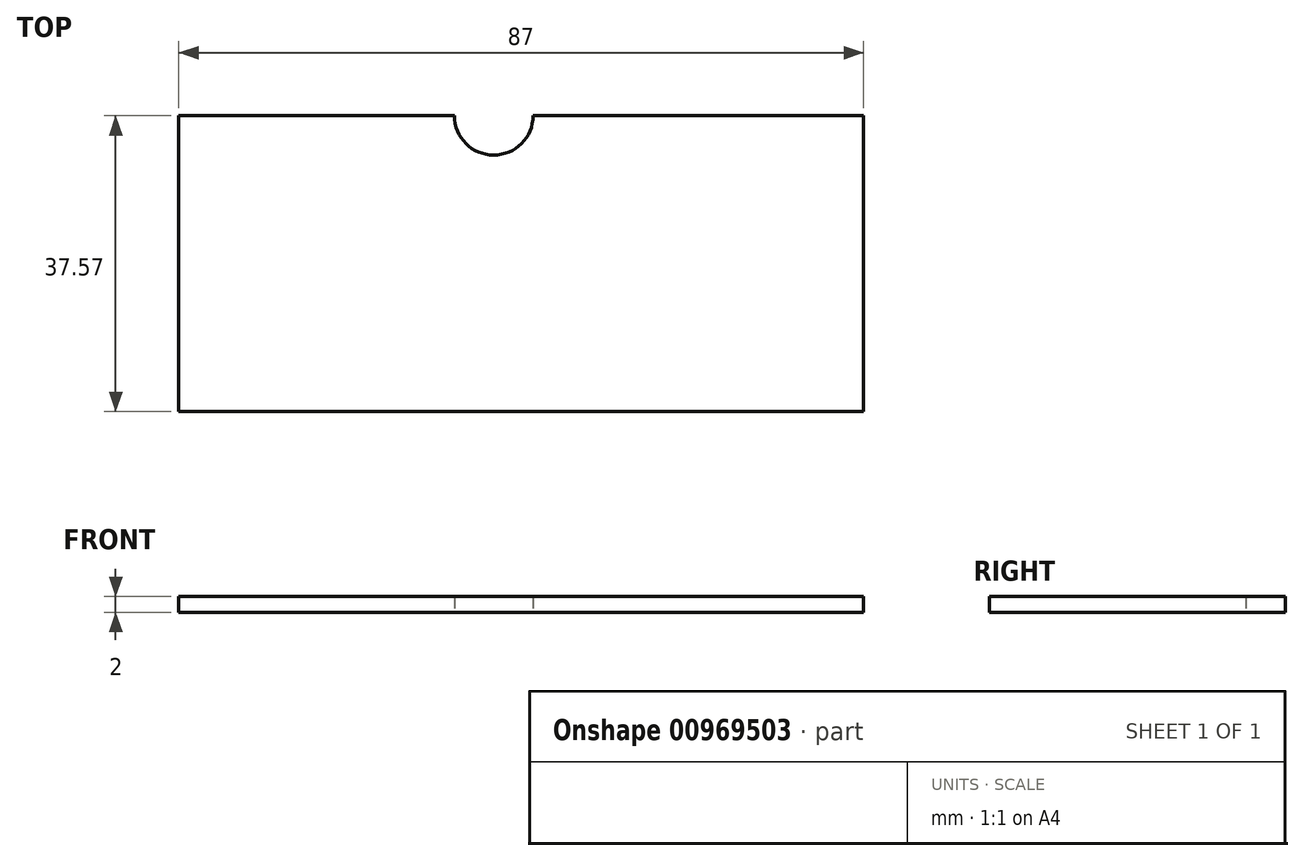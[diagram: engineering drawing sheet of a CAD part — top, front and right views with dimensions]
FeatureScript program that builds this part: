
annotation { "Feature Type Name" : "Feature", "Feature Type Description" : "" }
export const myFeature = defineFeature(function(context is Context, id is Id, definition is map)
    precondition{}
    {
        {
            var Q0;
            Q0=qCreatedBy(makeId("Top.planeOp"),FACE);
            var sketch = newSketch(context, id + "F0", { "sketchPlane" : qUnion([Q0])});
            skCircle(sketch, "E0", {"center": v(0, 0) * mm, "radius": 5 * mm});
            skCircle(sketch, "E1", {"center": v(0, 0) * mm, "radius": 35 * mm});
            skLineSegment(sketch, "E2.bottom", {"start": v(-40, 0) * mm, "end": v(47, 0) * mm});
            skLineSegment(sketch, "E2.top", {"start": v(-40, -37.57) * mm, "end": v(47, -37.57) * mm});
            skLineSegment(sketch, "E2.left", {"start": v(-40, 0) * mm, "end": v(-40, -37.57) * mm});
            skLineSegment(sketch, "E2.right", {"start": v(47, 0) * mm, "end": v(47, -37.57) * mm});
            skSolve(sketch);
        }
        {
            var Q0;
            Q0=makeQuery(id+"F0.imprint","IMPRINT",FACE,{"disambiguationData":[TD([[makeQuery(id+"F0.imprint","IMPRINT",EDGE,{"derivedFrom":sQuery(id+"F0.wireOp",EDGE,"E2.top")}),1.0]])]});
            var Q1;
            {var subQ0=sQuery(id+"F0.wireOp",EDGE,"E2.bottom");var subQ1=sQuery(id+"F0.wireOp",EDGE,"E0");var subQ2=makeQuery(id+"F0.imprint","INTERSECT",VERTEX,{"disambiguationData":[OD(0.0)],"derivedFrom":[subQ1,subQ0]});Q1=makeQuery(id+"F0.imprint","IMPRINT",FACE,{"disambiguationData":[TD([[makeQuery(id+"F0.imprint","IMPRINT",EDGE,{"disambiguationData":[TD([[subQ2,-1.0]])],"derivedFrom":subQ1}),-1.0]])]});}
            extrude(context, id + "F1", {"entities" : qUnion([Q0, Q1]), "depth" : 2 * mm, "offsetDistance" : 25 * mm});
        }
    });
